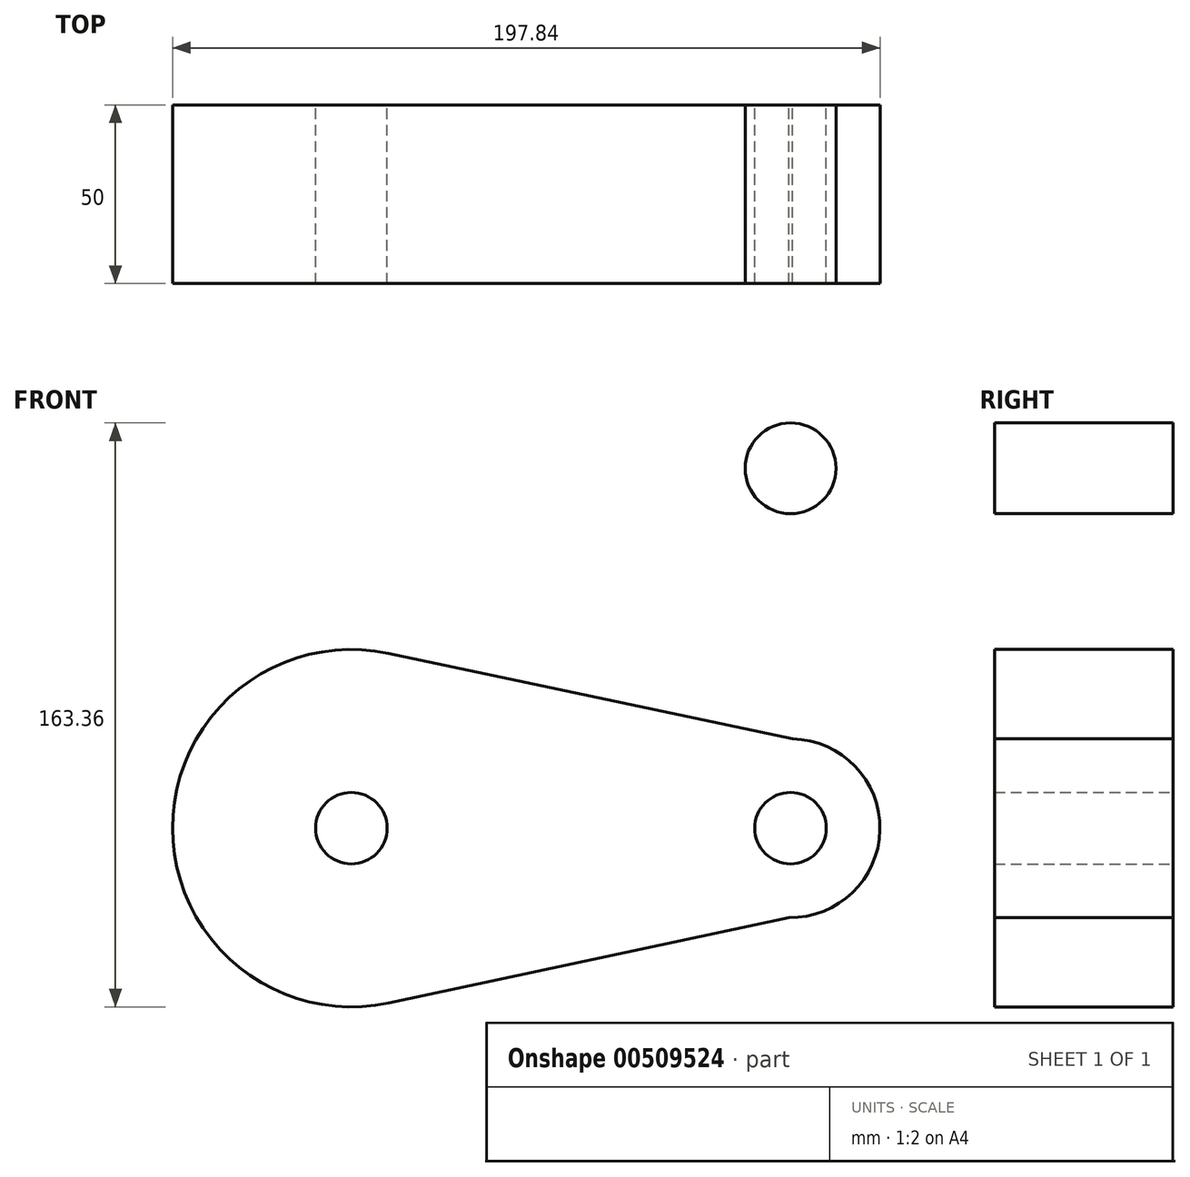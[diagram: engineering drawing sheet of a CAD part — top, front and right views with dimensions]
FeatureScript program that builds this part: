
annotation { "Feature Type Name" : "Feature", "Feature Type Description" : "" }
export const myFeature = defineFeature(function(context is Context, id is Id, definition is map)
    precondition{}
    {
        {
            var Q0;
            Q0=qCreatedBy(makeId("Front.planeOp"),FACE);
            var sketch = newSketch(context, id + "F0", { "sketchPlane" : qUnion([Q0])});
            skCircle(sketch, "E0", {"center": v(0, 0) * mm, "radius": 50 * mm});
            skCircle(sketch, "E1", {"center": v(122.84, 100.66) * mm, "radius": 12.7 * mm});
            skCircle(sketch, "E2", {"center": v(122.84, 0) * mm, "radius": 25 * mm});
            skLineSegment(sketch, "E3", {"start": v(10.35, 48.92) * mm, "end": v(123.37, 25) * mm});
            skLineSegment(sketch, "E4", {"start": v(10.45, -48.9) * mm, "end": v(122.34, -25) * mm});
            skCircle(sketch, "E5", {"center": v(0, 0) * mm, "radius": 10 * mm});
            skCircle(sketch, "E6", {"center": v(122.84, 0) * mm, "radius": 10 * mm});
            skSolve(sketch);
        }
        {
            var Q0;
            Q0 = qSketchRegion(id + "F0", true);
            extrude(context, id + "F1", {"entities" : qUnion([Q0]), "depth" : 50 * mm});
        }
    });
